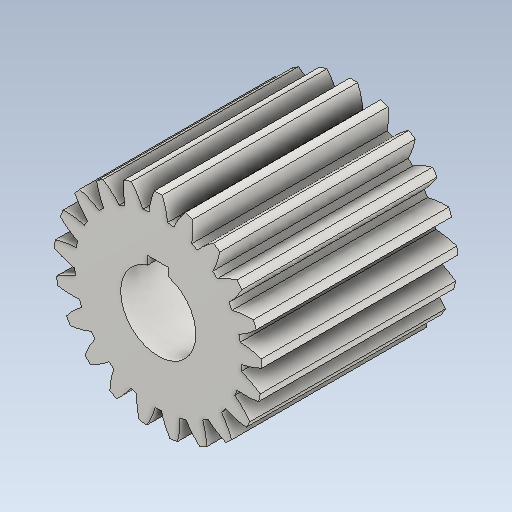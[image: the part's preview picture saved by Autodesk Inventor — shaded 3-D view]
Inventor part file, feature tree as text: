
AUTODESK INVENTOR PART (.ipt)
format: ipt  version: 2020 (Build 240168000, 168)  size: 307,200 bytes
history: native  units: mm (DEFAULTED — no unit token found)
features: plane x3, sketch x3, extrude x2, other x2
ambient origin geometry x8: Origin, YZ Plane, XZ Plane, XY Plane, X Axis, Y Axis, Z Axis, Center Point
bodies: Solid1 (feature_tree)
feature tree (10):
  extrude  "Extrusion1"  Depth=130.0mm TaperAngle=0.0deg
  plane  "Work Plane2"
  plane  "Work Plane8"
  plane  "Work Plane9"
  other  "正齿轮"
  extrude  "拉伸2"  Depth=10.0mm TaperAngle=0.0deg
  sketch  "Sketch1"  dims[d0=138.0mm d1=130.0mm d2=0.0mm]
  sketch  "Sketch2"  dims[d3=126.0mm d4=10.0mm d5=0.0mm]
  other  "Srf1"
  sketch  "草图3"  dims[d16=357.0mm d17=0.0mm d34=1.495997mm d39=0.0mm d41=0.0mm d43=357.0mm d46=357.0mm d47=0.0mm d48=0.0mm d49=50.0mm d50=14.0mm d51=9.0mm d52=3.5mm d53=10.0mm d54=0.0mm]
